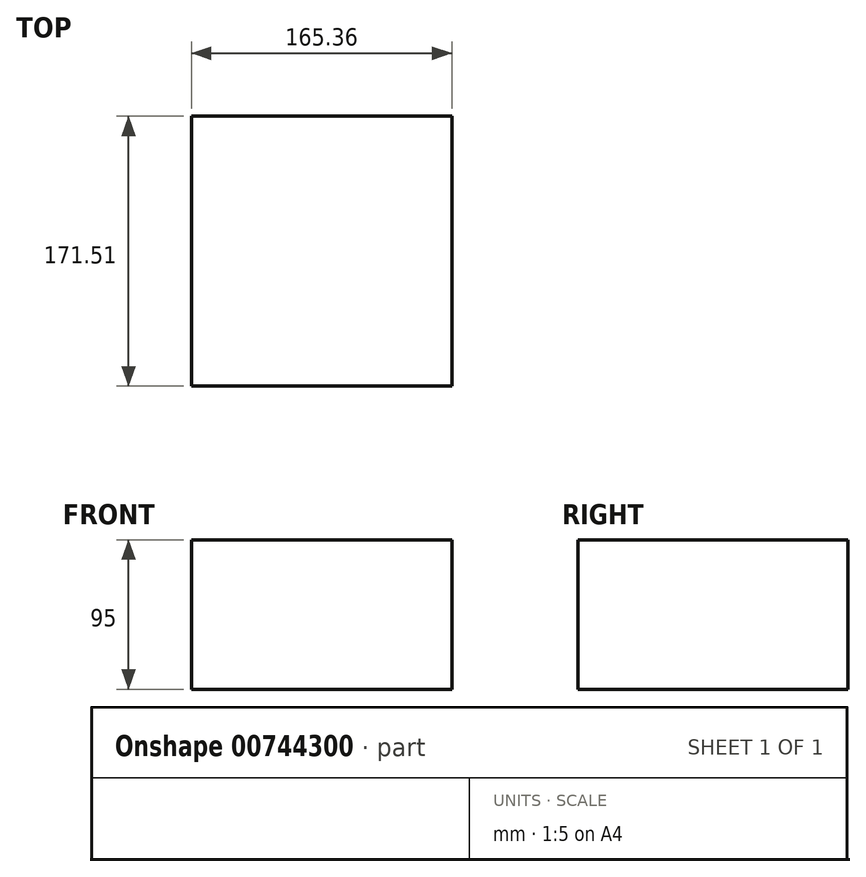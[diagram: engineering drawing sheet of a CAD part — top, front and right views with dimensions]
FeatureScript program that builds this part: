
annotation { "Feature Type Name" : "Feature", "Feature Type Description" : "" }
export const myFeature = defineFeature(function(context is Context, id is Id, definition is map)
    precondition{}
    {
        {
            var Q0;
            Q0=qCreatedBy(makeId("Top.planeOp"),FACE);
            var sketch = newSketch(context, id + "F0", { "sketchPlane" : qUnion([Q0])});
            skLineSegment(sketch, "E0.bottom", {"start": v(-81.38, 85.28) * mm, "end": v(83.98, 85.28) * mm});
            skLineSegment(sketch, "E0.top", {"start": v(-81.38, -86.23) * mm, "end": v(83.98, -86.23) * mm});
            skLineSegment(sketch, "E0.left", {"start": v(-81.38, 85.28) * mm, "end": v(-81.38, -86.23) * mm});
            skLineSegment(sketch, "E0.right", {"start": v(83.98, 85.28) * mm, "end": v(83.98, -86.23) * mm});
            skSolve(sketch);
        }
        {
            var Q0;
            Q0=makeQuery(id+"F0.imprint","IMPRINT",FACE,{"disambiguationData":[TD([[makeQuery(id+"F0.imprint","IMPRINT",EDGE,{"derivedFrom":sQuery(id+"F0.wireOp",EDGE,"E0.bottom")}),-1.0]])]});
            var sketch = newSketch(context, id + "F1", { "sketchPlane" : qUnion([Q0])});
            skCircle(sketch, "E1", {"center": v(0, 0) * mm, "radius": 60.05 * mm});
            skSolve(sketch);
        }
        {
            var Q0;
            Q0=makeQuery(id+"F1.imprint","IMPRINT",FACE,{"disambiguationData":[TD([[makeQuery(id+"F1.imprint","IMPRINT",EDGE,{"derivedFrom":sQuery(id+"F1.wireOp",EDGE,"E1")}),1.0]])]});
            var Q1;
            Q1=makeQuery(id+"F0.imprint","IMPRINT",FACE,{"disambiguationData":[TD([[makeQuery(id+"F0.imprint","IMPRINT",EDGE,{"derivedFrom":sQuery(id+"F0.wireOp",EDGE,"E0.bottom")}),-1.0]])]});
            var Q2;
            Q2=makeQuery(id+"F1.imprint","IMPRINT",FACE,{"disambiguationData":[TD([[makeQuery(id+"F1.imprint","IMPRINT",EDGE,{"derivedFrom":sQuery(id+"F1.wireOp",EDGE,"E1")}),-1.0]])]});
            extrude(context, id + "F2", {"entities" : qUnion([Q0, Q1, Q2]), "depth" : 95 * mm, "offsetDistance" : 25 * mm});
        }
    });
